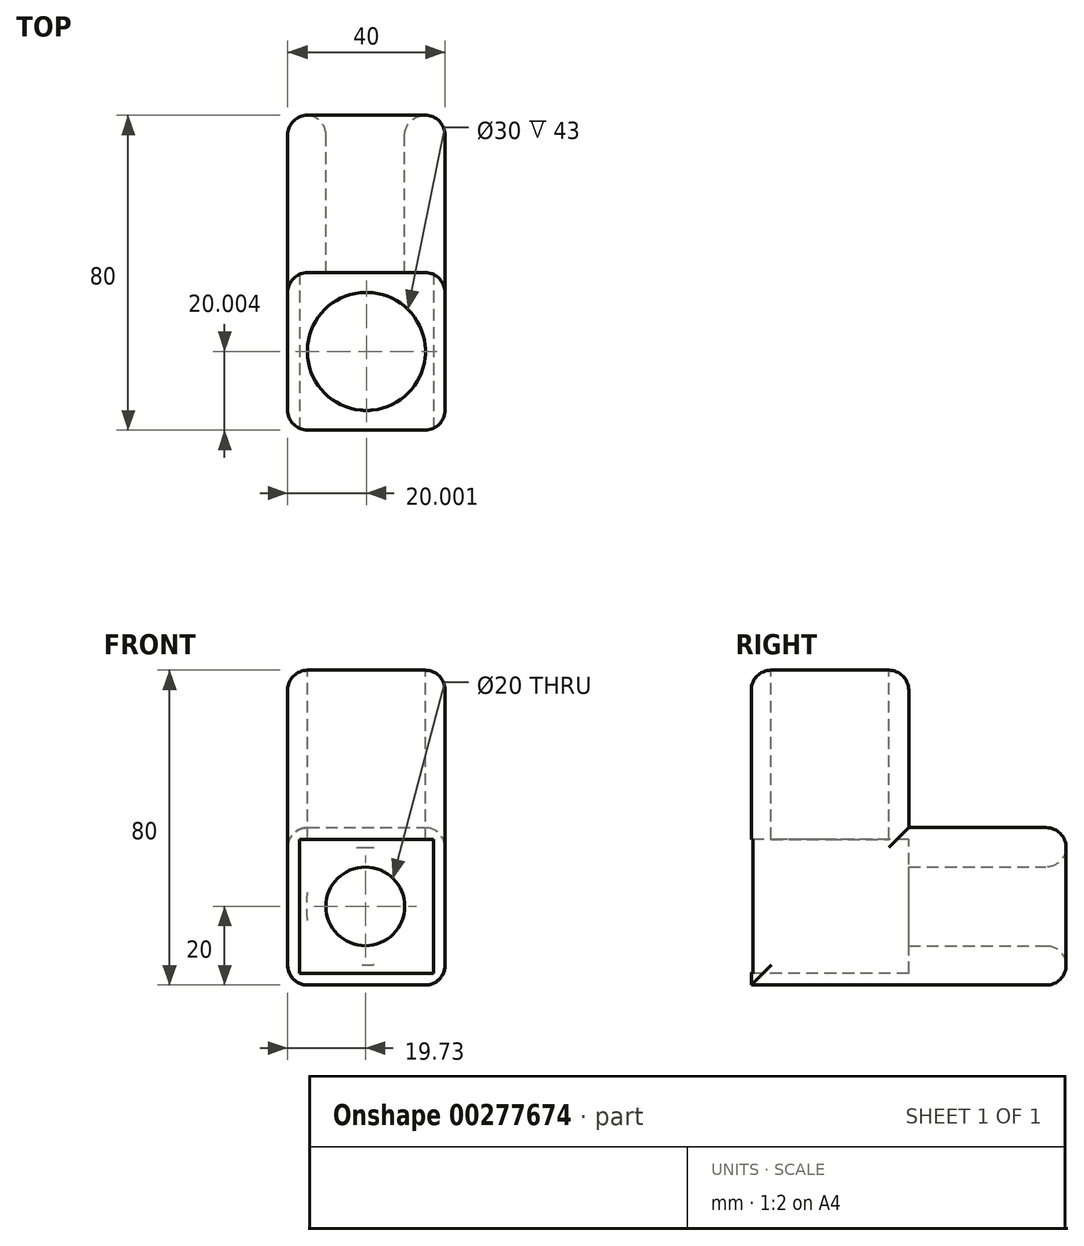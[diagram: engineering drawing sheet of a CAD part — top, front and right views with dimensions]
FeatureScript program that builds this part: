
annotation { "Feature Type Name" : "Feature", "Feature Type Description" : "" }
export const myFeature = defineFeature(function(context is Context, id is Id, definition is map)
    precondition{}
    {
        {
            var Q0;
            Q0=qCreatedBy(makeId("Top.planeOp"),FACE);
            var sketch = newSketch(context, id + "F0", { "sketchPlane" : qUnion([Q0])});
            skLineSegment(sketch, "E0.bottom", {"start": v(-19.73, 46.14) * mm, "end": v(20.27, 46.14) * mm});
            skLineSegment(sketch, "E0.top", {"start": v(-19.73, -33.86) * mm, "end": v(20.27, -33.86) * mm});
            skLineSegment(sketch, "E0.left", {"start": v(-19.73, 46.14) * mm, "end": v(-19.73, -33.86) * mm});
            skLineSegment(sketch, "E0.right", {"start": v(20.27, 46.14) * mm, "end": v(20.27, -33.86) * mm});
            skSolve(sketch);
        }
        {
            var Q0;
            Q0=makeQuery(id+"F0.imprint","IMPRINT",FACE,{"disambiguationData":[TD([[makeQuery(id+"F0.imprint","IMPRINT",EDGE,{"derivedFrom":sQuery(id+"F0.wireOp",EDGE,"E0.bottom")}),-1.0]])]});
            extrude(context, id + "F1", {"entities" : qUnion([Q0]), "depth" : 40 * mm});
        }
        {
            var Q0;
            Q0=makeQuery(id+"F1.opExtrude","CAP_FACE",FACE,{"disambiguationData":[OSD([sQuery(id+"F0.wireOp",EDGE,"E0.bottom"),sQuery(id+"F0.wireOp",EDGE,"E0.top"),sQuery(id+"F0.wireOp",EDGE,"E0.left"),sQuery(id+"F0.wireOp",EDGE,"E0.right")])],"isStart":false});
            var sketch = newSketch(context, id + "F2", { "sketchPlane" : qUnion([Q0])});
            skLineSegment(sketch, "E1.bottom", {"start": v(-19.73, -33.86) * mm, "end": v(20.27, -33.86) * mm});
            skLineSegment(sketch, "E1.top", {"start": v(-19.73, 6.14) * mm, "end": v(20.27, 6.14) * mm});
            skLineSegment(sketch, "E1.left", {"start": v(-19.73, -33.86) * mm, "end": v(-19.73, 6.14) * mm});
            skLineSegment(sketch, "E1.right", {"start": v(20.27, -33.86) * mm, "end": v(20.27, 6.14) * mm});
            skSolve(sketch);
        }
        {
            var Q0;
            Q0=makeQuery(id+"F2.imprint","IMPRINT",FACE,{"disambiguationData":[TD([[makeQuery(id+"F2.imprint","IMPRINT",EDGE,{"derivedFrom":sQuery(id+"F2.wireOp",EDGE,"E1.bottom")}),1.0]])]});
            extrude(context, id + "F3", {"entities" : qUnion([Q0]), "operationType" : NewBodyOperationType.ADD, "depth" : 40 * mm});
        }
        {
            var Q0;
            Q0=makeQuery(id+"F3.boolean.opBoolean","MERGE",FACE,{"derivedFrom":[makeQuery(id+"F1.opExtrude","SWEPT_FACE",FACE,{"disambiguationData":[OSD([sQuery(id+"F0.wireOp",EDGE,"E0.top")])]}),makeQuery(id+"F3.opExtrude","SWEPT_FACE",FACE,{"disambiguationData":[OSD([sQuery(id+"F2.wireOp",EDGE,"E1.bottom")])]})]});
            var sketch = newSketch(context, id + "F4", { "sketchPlane" : qUnion([Q0])});
            skLineSegment(sketch, "E2.bottom", {"start": v(-16.73, 3) * mm, "end": v(17.27, 3) * mm});
            skLineSegment(sketch, "E2.top", {"start": v(-16.73, 37) * mm, "end": v(17.27, 37) * mm});
            skLineSegment(sketch, "E2.left", {"start": v(-16.73, 3) * mm, "end": v(-16.73, 37) * mm});
            skLineSegment(sketch, "E2.right", {"start": v(17.27, 3) * mm, "end": v(17.27, 37) * mm});
            skSolve(sketch);
        }
        {
            var Q0;
            Q0=makeQuery(id+"F4.imprint","IMPRINT",FACE,{"disambiguationData":[TD([[makeQuery(id+"F4.imprint","IMPRINT",EDGE,{"derivedFrom":sQuery(id+"F4.wireOp",EDGE,"E2.bottom")}),1.0]])]});
            extrude(context, id + "F5", {"entities" : qUnion([Q0]), "operationType" : NewBodyOperationType.REMOVE, "oppositeDirection" : true, "depth" : 40 * mm});
        }
        {
            var Q0;
            Q0=makeQuery(id+"F3.opExtrude","CAP_FACE",FACE,{"disambiguationData":[OSD([sQuery(id+"F2.wireOp",EDGE,"E1.bottom"),sQuery(id+"F2.wireOp",EDGE,"E1.top"),sQuery(id+"F2.wireOp",EDGE,"E1.left"),sQuery(id+"F2.wireOp",EDGE,"E1.right")])],"isStart":false});
            var sketch = newSketch(context, id + "F6", { "sketchPlane" : qUnion([Q0])});
            skCircle(sketch, "E3", {"center": v(0.27, -13.86) * mm, "radius": 15 * mm});
            skPoint(sketch, "E3.centerSnap0", {"position": v(0.27, 6.14) * mm});
            skPoint(sketch, "E3.centerSnap1", {"position": v(-19.73, -13.86) * mm});
            skSolve(sketch);
        }
        {
            var Q0;
            Q0=makeQuery(id+"F6.imprint","IMPRINT",FACE,{"disambiguationData":[TD([[makeQuery(id+"F6.imprint","IMPRINT",EDGE,{"derivedFrom":sQuery(id+"F6.wireOp",EDGE,"E3")}),1.0]])]});
            extrude(context, id + "F7", {"entities" : qUnion([Q0]), "operationType" : NewBodyOperationType.REMOVE, "endBound" : BoundingType.UP_TO_NEXT, "oppositeDirection" : true, "depth" : 25.4 * mm});
        }
        {
            var Q0;
            Q0=makeQuery(id+"F1.opExtrude","SWEPT_FACE",FACE,{"disambiguationData":[OSD([sQuery(id+"F0.wireOp",EDGE,"E0.bottom")])]});
            var sketch = newSketch(context, id + "F8", { "sketchPlane" : qUnion([Q0])});
            skCircle(sketch, "E4", {"center": v(0, 20) * mm, "radius": 10 * mm});
            skPoint(sketch, "E4.centerSnap0", {"position": v(-20.27, 20) * mm});
            skSolve(sketch);
        }
        {
            var Q0;
            Q0 = qSketchRegion(id + "F8", true);
            extrude(context, id + "F9", {"entities" : qUnion([Q0]), "operationType" : NewBodyOperationType.REMOVE, "endBound" : BoundingType.THROUGH_ALL, "oppositeDirection" : true, "depth" : 25.4 * mm});
        }
        {
            var Q0;
            Q0=makeQuery(id+"F3.boolean.opBoolean","MERGE",FACE,{"derivedFrom":[makeQuery(id+"F1.opExtrude","SWEPT_FACE",FACE,{"disambiguationData":[OSD([sQuery(id+"F0.wireOp",EDGE,"E0.right")])]}),makeQuery(id+"F3.opExtrude","SWEPT_FACE",FACE,{"disambiguationData":[OSD([sQuery(id+"F2.wireOp",EDGE,"E1.right")])]})]});
            var Q1;
            Q1=makeQuery(id+"F3.boolean.opBoolean","MERGE",FACE,{"derivedFrom":[makeQuery(id+"F1.opExtrude","SWEPT_FACE",FACE,{"disambiguationData":[OSD([sQuery(id+"F0.wireOp",EDGE,"E0.left")])]}),makeQuery(id+"F3.opExtrude","SWEPT_FACE",FACE,{"disambiguationData":[OSD([sQuery(id+"F2.wireOp",EDGE,"E1.left")])]})]});
            var Q2;
            Q2=makeQuery(id+"F1.opExtrude","SWEPT_FACE",FACE,{"disambiguationData":[OSD([sQuery(id+"F0.wireOp",EDGE,"E0.bottom")])]});
            var Q3;
            Q3=makeQuery(id+"F3.opExtrude","CAP_EDGE",EDGE,{"disambiguationData":[OSD([sQuery(id+"F2.wireOp",EDGE,"E1.bottom")])],"isStart":false});
            var Q4;
            Q4=makeQuery(id+"F3.opExtrude","CAP_EDGE",EDGE,{"disambiguationData":[OSD([sQuery(id+"F2.wireOp",EDGE,"E1.top")])],"isStart":false});
            fillet(context, id + "F10", {"entities" : qUnion([Q0, Q1, Q2, Q3, Q4]), "radius" : 5.08 * mm, "tangentPropagation" : true, "allowEdgeOverflow" : false});
        }
    });
